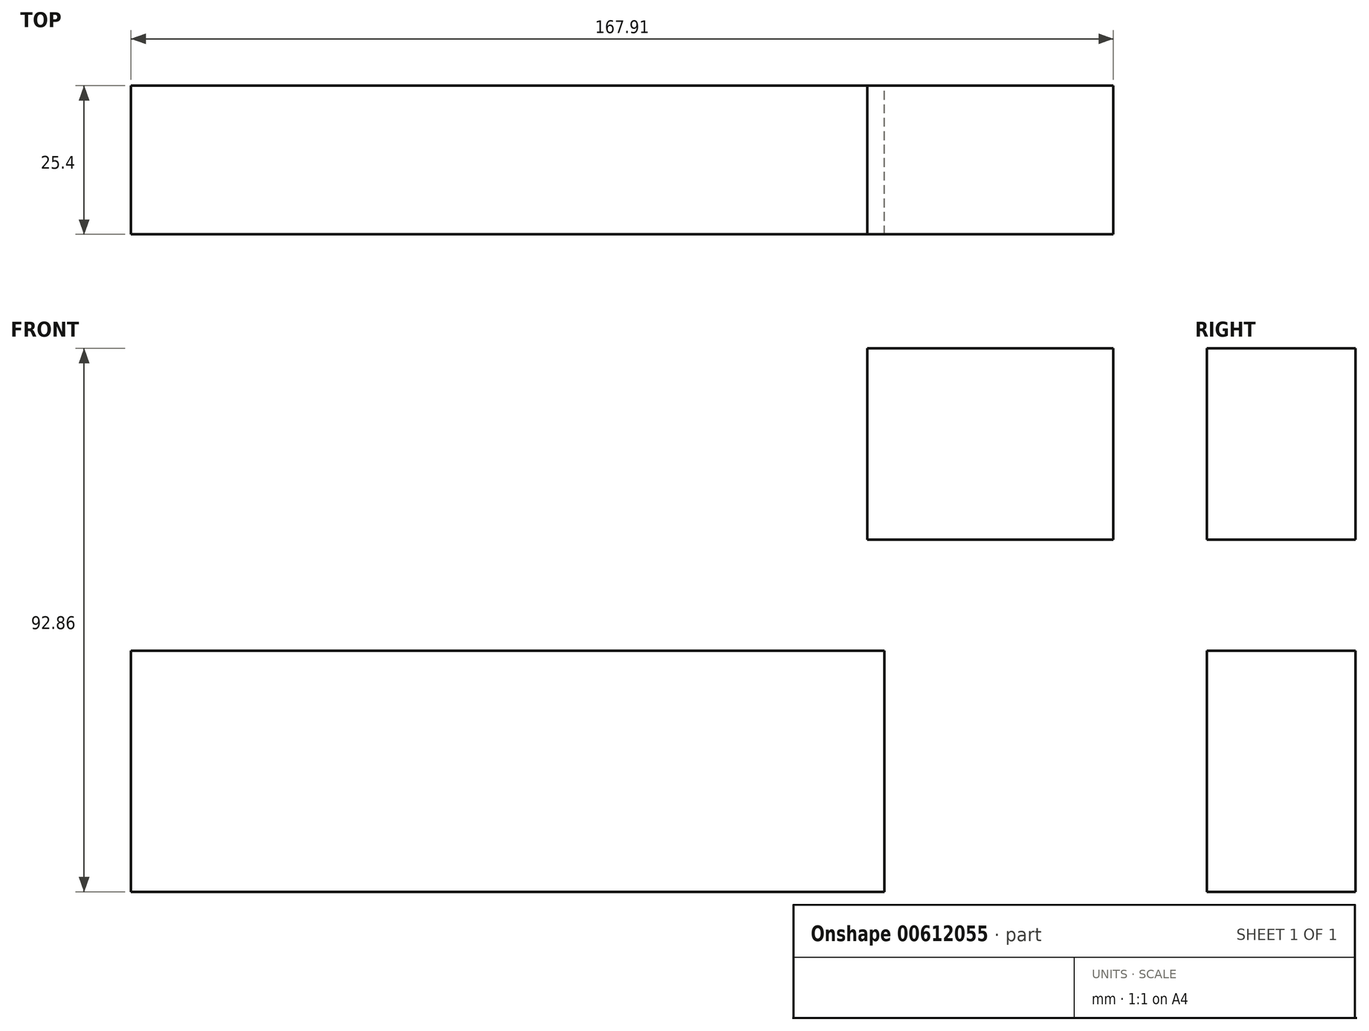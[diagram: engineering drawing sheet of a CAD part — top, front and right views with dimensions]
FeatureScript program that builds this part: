
annotation { "Feature Type Name" : "Feature", "Feature Type Description" : "" }
export const myFeature = defineFeature(function(context is Context, id is Id, definition is map)
    precondition{}
    {
        {
            var Q0;
            Q0=qCreatedBy(makeId("Front.planeOp"),FACE);
            var sketch = newSketch(context, id + "F0", { "sketchPlane" : qUnion([Q0])});
            skLineSegment(sketch, "E0.bottom", {"start": v(-64.39, -20.59) * mm, "end": v(64.39, -20.59) * mm});
            skLineSegment(sketch, "E0.top", {"start": v(-64.39, 20.59) * mm, "end": v(64.39, 20.59) * mm});
            skLineSegment(sketch, "E0.left", {"start": v(-64.39, -20.59) * mm, "end": v(-64.39, 20.59) * mm});
            skLineSegment(sketch, "E0.right", {"start": v(64.39, -20.59) * mm, "end": v(64.39, 20.59) * mm});
            skPoint(sketch, "E0.middle", {"position": v(0, 0) * mm});
            skLineSegment(sketch, "E1.bottom", {"start": v(103.52, 39.57) * mm, "end": v(61.47, 39.57) * mm});
            skLineSegment(sketch, "E1.top", {"start": v(103.52, 72.27) * mm, "end": v(61.47, 72.27) * mm});
            skLineSegment(sketch, "E1.left", {"start": v(103.52, 39.57) * mm, "end": v(103.52, 72.27) * mm});
            skLineSegment(sketch, "E1.right", {"start": v(61.47, 39.57) * mm, "end": v(61.47, 72.27) * mm});
            skPoint(sketch, "E1.middle", {"position": v(82.5, 55.92) * mm});
            skSolve(sketch);
        }
        {
            var Q0;
            Q0=qSketchRegion(id+"F0",true);
            extrude(context, id + "F1", {"entities" : qUnion([Q0]), "depth" : 25.4 * mm, "offsetDistance" : 25.4 * mm});
        }
    });
